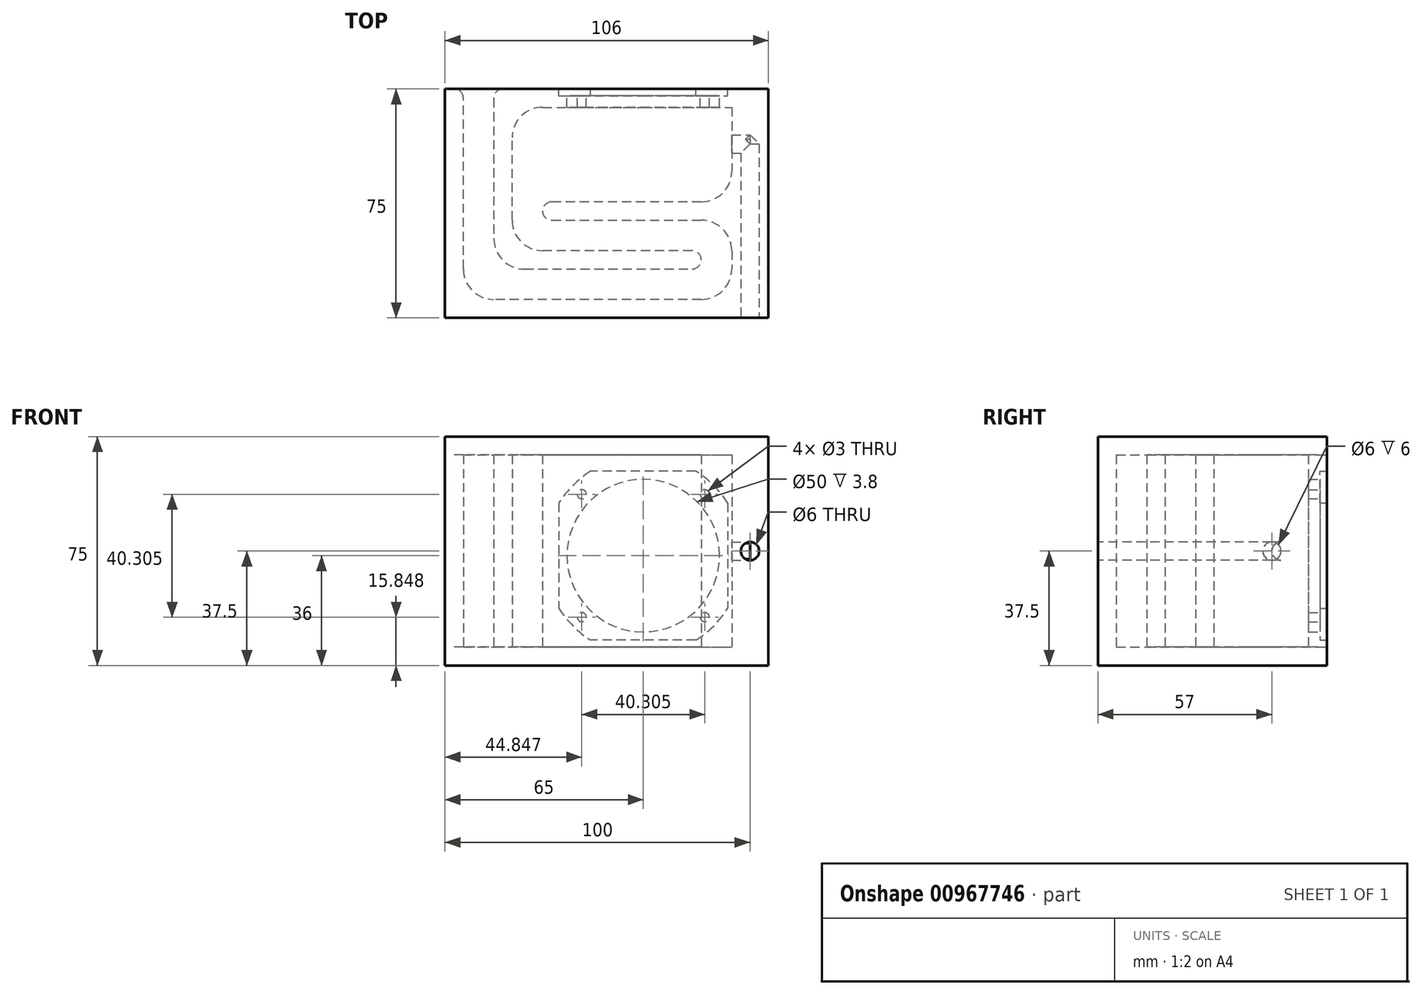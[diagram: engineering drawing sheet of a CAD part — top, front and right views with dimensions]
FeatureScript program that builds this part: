
annotation { "Feature Type Name" : "Feature", "Feature Type Description" : "" }
export const myFeature = defineFeature(function(context is Context, id is Id, definition is map)
    precondition{}
    {
        {
            assignVariable(context, id + "F0", {"variableType" : VariableType.LENGTH, "name" : "wall", "lengthValue" : 6 * mm});
        }
        {
            assignVariable(context, id + "F1", {"variableType" : VariableType.LENGTH, "name" : "line_depth", "lengthValue" : 10 * mm});
        }
        {
            assignVariable(context, id + "F2", {"variableType" : VariableType.LENGTH, "name" : "height", "lengthValue" : 75 * mm});
        }
        {
            var Q0;
            Q0=qCreatedBy(makeId("Top.planeOp"),FACE);
            var sketch = newSketch(context, id + "F3", { "sketchPlane" : qUnion([Q0])});
            skLineSegment(sketch, "E0", {"start": v(0, 0) * mm, "end": v(0, -75) * mm});
            skLineSegment(sketch, "E1", {"start": v(0, -75) * mm, "end": v(100, -75) * mm});
            skLineSegment(sketch, "E2", {"start": v(100, -75) * mm, "end": v(100, 0) * mm});
            skLineSegment(sketch, "E3", {"start": v(100, 0) * mm, "end": v(16, 0) * mm});
            skLineSegment(sketch, "E4", {"start": v(16, 0) * mm, "end": v(16, -59) * mm});
            skLineSegment(sketch, "E5", {"start": v(16, -59) * mm, "end": v(84, -59) * mm});
            skLineSegment(sketch, "E6", {"start": v(84, -59) * mm, "end": v(84, -53) * mm});
            skLineSegment(sketch, "E7", {"start": v(84, -53) * mm, "end": v(22, -53) * mm});
            skLineSegment(sketch, "E8", {"start": v(22, -53) * mm, "end": v(22, -6) * mm});
            skLineSegment(sketch, "E9", {"start": v(22, -6) * mm, "end": v(94, -6) * mm});
            skLineSegment(sketch, "E10", {"start": v(94, -6) * mm, "end": v(94, -37) * mm});
            skLineSegment(sketch, "E11", {"start": v(94, -37) * mm, "end": v(32, -37) * mm});
            skLineSegment(sketch, "E12", {"start": v(32, -37) * mm, "end": v(32, -43) * mm});
            skLineSegment(sketch, "E13", {"start": v(32, -43) * mm, "end": v(94, -43) * mm});
            skLineSegment(sketch, "E14", {"start": v(94, -43) * mm, "end": v(94, -69) * mm});
            skLineSegment(sketch, "E15", {"start": v(94, -69) * mm, "end": v(6, -69) * mm});
            skLineSegment(sketch, "E16", {"start": v(6, -69) * mm, "end": v(6, 0) * mm});
            skLineSegment(sketch, "E17", {"start": v(6, 0) * mm, "end": v(0, 0) * mm});
            skLineSegment(sketch, "E18", {"start": v(6, -29.5) * mm, "end": v(16, -29.5) * mm, "construction": true});
            skLineSegment(sketch, "E19", {"start": v(22, -40) * mm, "end": v(32, -40) * mm, "construction": true});
            skLineSegment(sketch, "E20", {"start": v(84, -56) * mm, "end": v(94, -56) * mm, "construction": true});
            skPoint(sketch, "E21", {"position": v(32, -40) * mm});
            skPoint(sketch, "E22", {"position": v(16, -29.5) * mm});
            skPoint(sketch, "E23", {"position": v(84, -56) * mm});
            skSolve(sketch);
        }
        {
            var Q0;
            Q0 = qSketchRegion(id + "F3", true);
            extrude(context, id + "F4", {"entities" : qUnion([Q0]), "depth" : getVariable(context, 'height') - 2 * getVariable(context, 'wall'), "offsetDistance" : 25 * mm});
        }
        {
            var Q0;
            Q0=makeQuery(id+"F4.opExtrude","SWEPT_EDGE",EDGE,{"disambiguationData":[OSD([sQuery(id+"F3.wireOp",EDGE,"E15"),sQuery(id+"F3.wireOp",EDGE,"E16")])]});
            var Q1;
            Q1=makeQuery(id+"F4.opExtrude","SWEPT_EDGE",EDGE,{"disambiguationData":[OSD([sQuery(id+"F3.wireOp",EDGE,"E14"),sQuery(id+"F3.wireOp",EDGE,"E15")])]});
            var Q2;
            Q2=makeQuery(id+"F4.opExtrude","SWEPT_EDGE",EDGE,{"disambiguationData":[OSD([sQuery(id+"F3.wireOp",EDGE,"E13"),sQuery(id+"F3.wireOp",EDGE,"E14")])]});
            var Q3;
            Q3=makeQuery(id+"F4.opExtrude","SWEPT_EDGE",EDGE,{"disambiguationData":[OSD([sQuery(id+"F3.wireOp",EDGE,"E10"),sQuery(id+"F3.wireOp",EDGE,"E11")])]});
            var Q4;
            Q4=makeQuery(id+"F4.opExtrude","SWEPT_EDGE",EDGE,{"disambiguationData":[OSD([sQuery(id+"F3.wireOp",EDGE,"E7"),sQuery(id+"F3.wireOp",EDGE,"E8")])]});
            var Q5;
            Q5=makeQuery(id+"F4.opExtrude","SWEPT_EDGE",EDGE,{"disambiguationData":[OSD([sQuery(id+"F3.wireOp",EDGE,"E4"),sQuery(id+"F3.wireOp",EDGE,"E5")])]});
            var Q6;
            Q6=makeQuery(id+"F4.opExtrude","SWEPT_EDGE",EDGE,{"disambiguationData":[OSD([sQuery(id+"F3.wireOp",EDGE,"E8"),sQuery(id+"F3.wireOp",EDGE,"E9")])]});
            fillet(context, id + "F5", {"entities" : qUnion([Q0, Q1, Q2, Q3, Q4, Q5, Q6]), "tangentPropagation" : true, "radius" : getVariable(context, 'line_depth'), "defaultsChanged" : false, "vertexSettings" : [], "allowEdgeOverflow" : false});
        }
        {
            var Q0;
            Q0=makeQuery(id+"F4.opExtrude","SWEPT_FACE",FACE,{"disambiguationData":[OSD([sQuery(id+"F3.wireOp",EDGE,"E3")])]});
            var sketch = newSketch(context, id + "F6", { "sketchPlane" : qUnion([Q0])});
            skCircle(sketch, "E24", {"center": v(-65, 30) * mm, "radius": 25 * mm});
            skCircle(sketch, "E25", {"center": v(-85.15, 9.85) * mm, "radius": 1.5 * mm});
            skCircle(sketch, "E26", {"center": v(-85.15, 50.15) * mm, "radius": 1.5 * mm});
            skCircle(sketch, "E27", {"center": v(-44.85, 9.85) * mm, "radius": 1.5 * mm});
            skCircle(sketch, "E28", {"center": v(-44.85, 50.15) * mm, "radius": 1.5 * mm});
            skLineSegment(sketch, "E29.bottom", {"start": v(-85.15, 9.85) * mm, "end": v(-44.85, 9.85) * mm, "construction": true});
            skLineSegment(sketch, "E29.top", {"start": v(-85.15, 50.15) * mm, "end": v(-44.85, 50.15) * mm, "construction": true});
            skLineSegment(sketch, "E29.left", {"start": v(-85.15, 9.85) * mm, "end": v(-85.15, 50.15) * mm, "construction": true});
            skLineSegment(sketch, "E29.right", {"start": v(-44.85, 9.85) * mm, "end": v(-44.85, 50.15) * mm, "construction": true});
            skPoint(sketch, "E30", {"position": v(-44.85, 30) * mm});
            skPoint(sketch, "E31", {"position": v(-65, 50.15) * mm});
            skSolve(sketch);
        }
        {
            var Q0;
            Q0 = qSketchRegion(id + "F6", true);
            extrude(context, id + "F7", {"entities" : qUnion([Q0]), "operationType" : NewBodyOperationType.REMOVE, "oppositeDirection" : true, "depth" : 10 * mm, "offsetDistance" : 25 * mm});
        }
        {
            var Q0;
            Q0=makeQuery(id+"F4.opExtrude","SWEPT_EDGE",EDGE,{"disambiguationData":[OSD([sQuery(id+"F3.wireOp",EDGE,"E6"),sQuery(id+"F3.wireOp",EDGE,"E7")])]});
            var Q1;
            Q1=makeQuery(id+"F4.opExtrude","SWEPT_EDGE",EDGE,{"disambiguationData":[OSD([sQuery(id+"F3.wireOp",EDGE,"E5"),sQuery(id+"F3.wireOp",EDGE,"E6")])]});
            var Q2;
            Q2=makeQuery(id+"F4.opExtrude","SWEPT_EDGE",EDGE,{"disambiguationData":[OSD([sQuery(id+"F3.wireOp",EDGE,"E12"),sQuery(id+"F3.wireOp",EDGE,"E13")])]});
            var Q3;
            Q3=makeQuery(id+"F4.opExtrude","SWEPT_EDGE",EDGE,{"disambiguationData":[OSD([sQuery(id+"F3.wireOp",EDGE,"E11"),sQuery(id+"F3.wireOp",EDGE,"E12")])]});
            var Q4;
            Q4=makeQuery(id+"F4.opExtrude","SWEPT_EDGE",EDGE,{"disambiguationData":[OSD([sQuery(id+"F3.wireOp",EDGE,"E3"),sQuery(id+"F3.wireOp",EDGE,"E4")])]});
            var Q5;
            Q5=makeQuery(id+"F4.opExtrude","SWEPT_EDGE",EDGE,{"disambiguationData":[OSD([sQuery(id+"F3.wireOp",EDGE,"E16"),sQuery(id+"F3.wireOp",EDGE,"E17")])]});
            fillet(context, id + "F8", {"entities" : qUnion([Q0, Q1, Q2, Q3, Q4, Q5]), "tangentPropagation" : true, "radius" : 3 * mm, "defaultsChanged" : true, "vertexSettings" : [], "allowEdgeOverflow" : false});
        }
        {
            var Q0;
            Q0=makeQuery(id+"F4.opExtrude","SWEPT_FACE",FACE,{"disambiguationData":[OSD([sQuery(id+"F3.wireOp",EDGE,"E3")])]});
            var sketch = newSketch(context, id + "F9", { "sketchPlane" : qUnion([Q0])});
            skCircle(sketch, "E32", {"center": v(-65, 30) * mm, "radius": 32.6 * mm, "construction": true});
            skLineSegment(sketch, "E33", {"start": v(-92.66, 47.25) * mm, "end": v(-92.66, 12.75) * mm});
            skLineSegment(sketch, "E34", {"start": v(-37.34, 47.25) * mm, "end": v(-37.34, 12.75) * mm});
            skLineSegment(sketch, "E35", {"start": v(-82.25, 57.66) * mm, "end": v(-47.75, 57.66) * mm});
            skLineSegment(sketch, "E36", {"start": v(-82.25, 2.34) * mm, "end": v(-47.75, 2.34) * mm});
            skArc(sketch, "E37", {"start": v(-82.25, 57.66) * mm, "mid": v(-88.05, 53.05) * mm, "end": v(-92.66, 47.25) * mm});
            skArc(sketch, "E38", {"start": v(-37.34, 47.25) * mm, "mid": v(-41.95, 53.05) * mm, "end": v(-47.75, 57.66) * mm});
            skArc(sketch, "E39", {"start": v(-47.75, 2.34) * mm, "mid": v(-41.95, 6.95) * mm, "end": v(-37.34, 12.75) * mm});
            skArc(sketch, "E40", {"start": v(-92.66, 12.75) * mm, "mid": v(-88.05, 6.95) * mm, "end": v(-82.25, 2.34) * mm});
            skSolve(sketch);
        }
        {
            var Q0;
            Q0 = qSketchRegion(id + "F9", true);
            extrude(context, id + "F10", {"entities" : qUnion([Q0]), "operationType" : NewBodyOperationType.REMOVE, "oppositeDirection" : true, "depth" : 2.2 * mm, "offsetDistance" : 25 * mm});
        }
        {
            var Q0;
            Q0=makeQuery(id+"F4.opExtrude","SWEPT_FACE",FACE,{"disambiguationData":[OSD([sQuery(id+"F3.wireOp",EDGE,"E2")])]});
            var sketch = newSketch(context, id + "F11", { "sketchPlane" : qUnion([Q0])});
            skCircle(sketch, "E41", {"center": v(-18, 31.5) * mm, "radius": 3 * mm});
            skSolve(sketch);
        }
        {
            var Q0;
            Q0 = qSketchRegion(id + "F11", true);
            var Q1;
            Q1=sQuery(id+"F11.wireOp",EDGE,"E41");
            extrude(context, id + "F12", {"entities" : qUnion([Q0]), "operationType" : NewBodyOperationType.REMOVE, "surfaceEntities" : qUnion([Q1]), "oppositeDirection" : true, "depth" : 10 * mm, "offsetDistance" : 25 * mm});
        }
        {
            var Q0;
            Q0=makeQuery(id+"F4.opExtrude","CAP_FACE",FACE,{"disambiguationData":[OSD([sQuery(id+"F3.wireOp",EDGE,"E0"),sQuery(id+"F3.wireOp",EDGE,"E1"),sQuery(id+"F3.wireOp",EDGE,"E2"),sQuery(id+"F3.wireOp",EDGE,"E3"),sQuery(id+"F3.wireOp",EDGE,"E4"),sQuery(id+"F3.wireOp",EDGE,"E5"),sQuery(id+"F3.wireOp",EDGE,"E6"),sQuery(id+"F3.wireOp",EDGE,"E7"),sQuery(id+"F3.wireOp",EDGE,"E8"),sQuery(id+"F3.wireOp",EDGE,"E9"),sQuery(id+"F3.wireOp",EDGE,"E10"),sQuery(id+"F3.wireOp",EDGE,"E11"),sQuery(id+"F3.wireOp",EDGE,"E12"),sQuery(id+"F3.wireOp",EDGE,"E13"),sQuery(id+"F3.wireOp",EDGE,"E14"),sQuery(id+"F3.wireOp",EDGE,"E15"),sQuery(id+"F3.wireOp",EDGE,"E16"),sQuery(id+"F3.wireOp",EDGE,"E17")])],"isStart":true});
            var sketch = newSketch(context, id + "F13", { "sketchPlane" : qUnion([Q0])});
            skLineSegment(sketch, "E42.bottom", {"start": v(100, 75) * mm, "end": v(0, 75) * mm});
            skLineSegment(sketch, "E42.top", {"start": v(100, 0) * mm, "end": v(0, 0) * mm});
            skLineSegment(sketch, "E42.left", {"start": v(100, 75) * mm, "end": v(100, 0) * mm});
            skLineSegment(sketch, "E42.right", {"start": v(0, 75) * mm, "end": v(0, 0) * mm});
            skSolve(sketch);
        }
        {
            var Q0;
            Q0 = qSketchRegion(id + "F13", true);
            extrude(context, id + "F14", {"entities" : qUnion([Q0]), "operationType" : NewBodyOperationType.ADD, "depth" : getVariable(context, 'wall'), "offsetDistance" : 25 * mm});
        }
        {
            var Q0;
            Q0=makeQuery(id+"F4.opExtrude","CAP_FACE",FACE,{"disambiguationData":[OSD([sQuery(id+"F3.wireOp",EDGE,"E0"),sQuery(id+"F3.wireOp",EDGE,"E1"),sQuery(id+"F3.wireOp",EDGE,"E2"),sQuery(id+"F3.wireOp",EDGE,"E3"),sQuery(id+"F3.wireOp",EDGE,"E4"),sQuery(id+"F3.wireOp",EDGE,"E5"),sQuery(id+"F3.wireOp",EDGE,"E6"),sQuery(id+"F3.wireOp",EDGE,"E7"),sQuery(id+"F3.wireOp",EDGE,"E8"),sQuery(id+"F3.wireOp",EDGE,"E9"),sQuery(id+"F3.wireOp",EDGE,"E10"),sQuery(id+"F3.wireOp",EDGE,"E11"),sQuery(id+"F3.wireOp",EDGE,"E12"),sQuery(id+"F3.wireOp",EDGE,"E13"),sQuery(id+"F3.wireOp",EDGE,"E14"),sQuery(id+"F3.wireOp",EDGE,"E15"),sQuery(id+"F3.wireOp",EDGE,"E16"),sQuery(id+"F3.wireOp",EDGE,"E17")])],"isStart":false});
            var sketch = newSketch(context, id + "F15", { "sketchPlane" : qUnion([Q0])});
            skLineSegment(sketch, "E43.bottom", {"start": v(100, 0) * mm, "end": v(0, 0) * mm});
            skLineSegment(sketch, "E43.top", {"start": v(100, -75) * mm, "end": v(0, -75) * mm});
            skLineSegment(sketch, "E43.left", {"start": v(100, 0) * mm, "end": v(100, -75) * mm});
            skLineSegment(sketch, "E43.right", {"start": v(0, 0) * mm, "end": v(0, -75) * mm});
            skSolve(sketch);
        }
        {
            var Q0;
            Q0 = qSketchRegion(id + "F15", true);
            extrude(context, id + "F16", {"entities" : qUnion([Q0]), "operationType" : NewBodyOperationType.ADD, "depth" : getVariable(context, 'wall'), "offsetDistance" : 25 * mm});
        }
        {
            var Q0;
            Q0=makeQuery(id+"F16.boolean.opBoolean","MERGE",FACE,{"derivedFrom":[makeQuery(id+"F14.boolean.opBoolean","MERGE",FACE,{"derivedFrom":[makeQuery(id+"F4.opExtrude","SWEPT_FACE",FACE,{"disambiguationData":[OSD([sQuery(id+"F3.wireOp",EDGE,"E1")])]}),makeQuery(id+"F14.opExtrude","SWEPT_FACE",FACE,{"disambiguationData":[OSD([sQuery(id+"F13.wireOp",EDGE,"E42.bottom")])]})]}),makeQuery(id+"F16.opExtrude","SWEPT_FACE",FACE,{"disambiguationData":[OSD([sQuery(id+"F15.wireOp",EDGE,"E43.top")])]})]});
            var sketch = newSketch(context, id + "F17", { "sketchPlane" : qUnion([Q0])});
            skLineSegment(sketch, "E44.bottom", {"start": v(100, 69) * mm, "end": v(106, 69) * mm});
            skLineSegment(sketch, "E44.top", {"start": v(100, -6) * mm, "end": v(106, -6) * mm});
            skLineSegment(sketch, "E44.left", {"start": v(100, 69) * mm, "end": v(100, -6) * mm});
            skLineSegment(sketch, "E44.right", {"start": v(106, 69) * mm, "end": v(106, -6) * mm});
            skSolve(sketch);
        }
        {
            var Q0;
            Q0 = qSketchRegion(id + "F17", true);
            var Q1;
            Q1=makeQuery(id+"F16.boolean.opBoolean","MERGE",FACE,{"derivedFrom":[makeQuery(id+"F14.boolean.opBoolean","MERGE",FACE,{"derivedFrom":[makeQuery(id+"F4.opExtrude","SWEPT_FACE",FACE,{"disambiguationData":[OSD([sQuery(id+"F3.wireOp",EDGE,"E17")])]}),makeQuery(id+"F4.opExtrude","SWEPT_FACE",FACE,{"disambiguationData":[OSD([sQuery(id+"F3.wireOp",EDGE,"E3")])]}),makeQuery(id+"F14.opExtrude","SWEPT_FACE",FACE,{"disambiguationData":[OSD([sQuery(id+"F13.wireOp",EDGE,"E42.top")])]})]}),makeQuery(id+"F16.opExtrude","SWEPT_FACE",FACE,{"disambiguationData":[OSD([sQuery(id+"F15.wireOp",EDGE,"E43.bottom")])]})]});
            extrude(context, id + "F18", {"entities" : qUnion([Q0]), "operationType" : NewBodyOperationType.ADD, "endBound" : BoundingType.UP_TO_SURFACE, "oppositeDirection" : true, "depth" : 25 * mm, "endBoundEntityFace" : qUnion([Q1]), "offsetDistance" : 25 * mm});
        }
        {
            var Q0;
            Q0=makeQuery(id+"F18.boolean.opBoolean","MERGE",FACE,{"derivedFrom":[makeQuery(id+"F16.boolean.opBoolean","MERGE",FACE,{"derivedFrom":[makeQuery(id+"F14.boolean.opBoolean","MERGE",FACE,{"derivedFrom":[makeQuery(id+"F4.opExtrude","SWEPT_FACE",FACE,{"disambiguationData":[OSD([sQuery(id+"F3.wireOp",EDGE,"E1")])]}),makeQuery(id+"F14.opExtrude","SWEPT_FACE",FACE,{"disambiguationData":[OSD([sQuery(id+"F13.wireOp",EDGE,"E42.bottom")])]})]}),makeQuery(id+"F16.opExtrude","SWEPT_FACE",FACE,{"disambiguationData":[OSD([sQuery(id+"F15.wireOp",EDGE,"E43.top")])]})]}),makeQuery(id+"F18.opExtrude","CAP_FACE",FACE,{"disambiguationData":[OSD([sQuery(id+"F17.wireOp",EDGE,"E44.bottom"),sQuery(id+"F17.wireOp",EDGE,"E44.top"),sQuery(id+"F17.wireOp",EDGE,"E44.left"),sQuery(id+"F17.wireOp",EDGE,"E44.right")])],"isStart":true})]});
            var sketch = newSketch(context, id + "F19", { "sketchPlane" : qUnion([Q0])});
            skCircle(sketch, "E45", {"center": v(100, 31.5) * mm, "radius": 3 * mm});
            skSolve(sketch);
        }
        {
            var Q0;
            Q0=makeQuery(id+"F19.imprint","IMPRINT",FACE,{"disambiguationData":[TD([[makeQuery(id+"F19.imprint","IMPRINT",EDGE,{"derivedFrom":sQuery(id+"F19.wireOp",EDGE,"E45")}),1.0]])]});
            var Q1;
            Q1=makeQuery(id+"F12.boolean.opBoolean","COPY",FACE,{"derivedFrom":makeQuery(id+"F12.opExtrude","SWEPT_FACE",FACE,{"disambiguationData":[OSD([sQuery(id+"F11.wireOp",EDGE,"E41")])]})});
            extrude(context, id + "F20", {"entities" : qUnion([Q0]), "operationType" : NewBodyOperationType.REMOVE, "endBound" : BoundingType.UP_TO_SURFACE, "oppositeDirection" : true, "depth" : 25 * mm, "endBoundEntityFace" : qUnion([Q1]), "hasOffset" : true, "offsetDistance" : -3 * mm});
        }
    });
